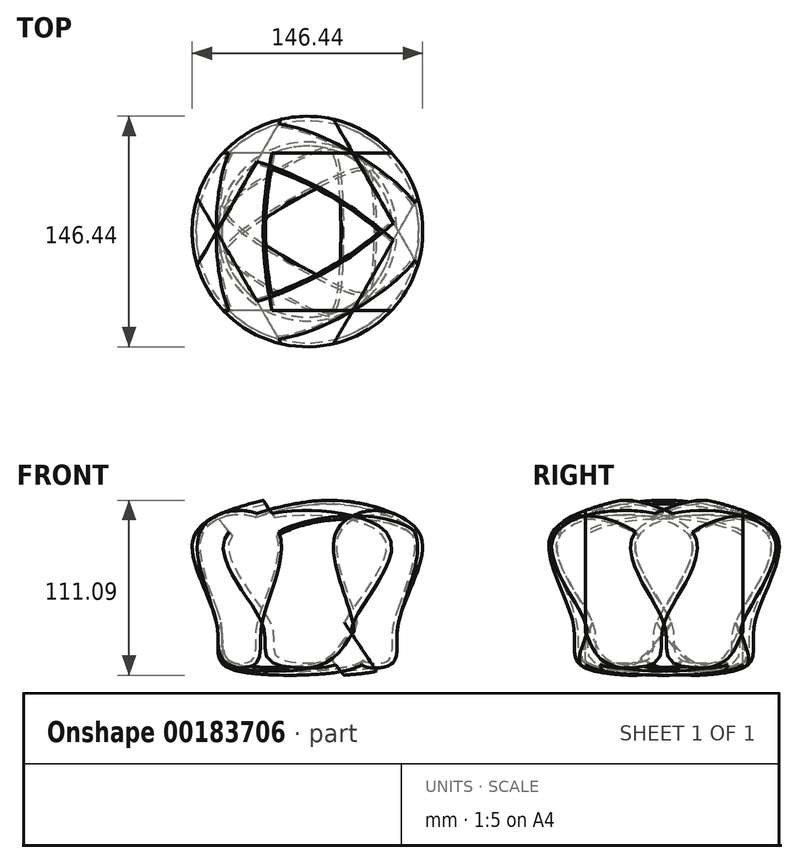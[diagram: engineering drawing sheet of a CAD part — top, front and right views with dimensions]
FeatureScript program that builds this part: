
annotation { "Feature Type Name" : "Feature", "Feature Type Description" : "" }
export const myFeature = defineFeature(function(context is Context, id is Id, definition is map)
    precondition{}
    {
        {
            var Q0;
            Q0=qCreatedBy(makeId("Front.planeOp"),FACE);
            var sketch = newSketch(context, id + "F0", { "sketchPlane" : qUnion([Q0])});
            skLineSegment(sketch, "E0", {"start": v(0, 0) * mm, "end": v(22.16, 0) * mm});
            skLineSegment(sketch, "E1", {"start": v(0, 112.85) * mm, "end": v(21.44, 112.85) * mm});
            skLineSegment(sketch, "E2", {"start": v(0, 112.85) * mm, "end": v(0, 0) * mm});
            skFitSpline(sketch, "E3", {"points": [v(21.44, 112.85) * mm, v(72.62, 86.57) * mm, v(57.75, 33.31) * mm, v(54.64, 8.07) * mm, v(22.16, 0) * mm], "startDerivative": vector(241.93, -60.5) * mm, "endDerivative": vector(-187.13, -14.65) * mm});
            skSolve(sketch);
        }
        {
            var Q0;
            Q0=makeQuery(id+"F0.imprint","IMPRINT",FACE,{"disambiguationData":[TD([[makeQuery(id+"F0.imprint","IMPRINT",EDGE,{"derivedFrom":sQuery(id+"F0.wireOp",EDGE,"E0")}),1.0]])]});
            var Q1;
            Q1=sQuery(id+"F0.wireOp",EDGE,"E2");
            revolve(context, id + "F1", {"entities" : qUnion([Q0]), "axis" : qUnion([Q1]), "revolveType" : RevolveType.FULL});
        }
        {
            var Q0;
            Q0=makeQuery(id+"F1.opRevolve","SWEPT_FACE",FACE,{"disambiguationData":[OSD([sQuery(id+"F0.wireOp",EDGE,"E1")])]});
            shell(context, id + "F2", {"entities" : qUnion([Q0]), "thickness" : 2.54 * mm});
        }
        {
            var Q0;
            Q0=qCreatedBy(makeId("Front.planeOp"),FACE);
            var sketch = newSketch(context, id + "F3", { "sketchPlane" : qUnion([Q0])});
            skLineSegment(sketch, "E4", {"start": v(-47.72, 140.74) * mm, "end": v(60.17, -21.79) * mm});
            skLineSegment(sketch, "E5", {"start": v(60.17, -21.79) * mm, "end": v(158.38, 59.13) * mm});
            skLineSegment(sketch, "E6", {"start": v(158.38, 59.13) * mm, "end": v(16.6, 153.88) * mm});
            skLineSegment(sketch, "E7", {"start": v(16.6, 153.88) * mm, "end": v(-47.72, 140.74) * mm});
            skLineSegment(sketch, "E8", {"start": v(-87.83, 138.67) * mm, "end": v(62.25, -48.76) * mm});
            skLineSegment(sketch, "E9", {"start": v(62.25, -48.76) * mm, "end": v(-161.84, -48.76) * mm});
            skLineSegment(sketch, "E10", {"start": v(-161.84, -48.76) * mm, "end": v(-87.83, 138.67) * mm});
            skSolve(sketch);
        }
        {
            var Q0;
            Q0 = qSketchRegion(id + "F3", true);
            extrude(context, id + "F4", {"entities" : qUnion([Q0]), "operationType" : NewBodyOperationType.REMOVE, "endBound" : BoundingType.SYMMETRIC, "oppositeDirection" : true, "depth" : 100 * mm});
        }
        {
            var Q0;
            Q0=qCreatedBy(makeId("Right.planeOp"),FACE);
            var sketch = newSketch(context, id + "F5", { "sketchPlane" : qUnion([Q0])});
            skLineSegment(sketch, "E11", {"start": v(0, 29.4) * mm, "end": v(0, 175.32) * mm, "construction": true});
            skSolve(sketch);
        }
        {
            var Q0;
            Q0=makeQuery(id+"F1.opRevolve","SWEPT_BODY",BODY,{"disambiguationData":[OSD([sQuery(id+"F0.wireOp",EDGE,"E0"),sQuery(id+"F0.wireOp",EDGE,"E1"),sQuery(id+"F0.wireOp",EDGE,"E2"),sQuery(id+"F0.wireOp",EDGE,"E3")])]});
            var Q1;
            Q1=sQuery(id+"F5.wireOp",EDGE,"E11");
            circularPattern(context, id + "F6", {"entities" : qUnion([Q0]), "axis" : qUnion([Q1]), "angle" : 120 * degree, "instanceCount" : 3, "oppositeDirection" : true});
        }
    });
